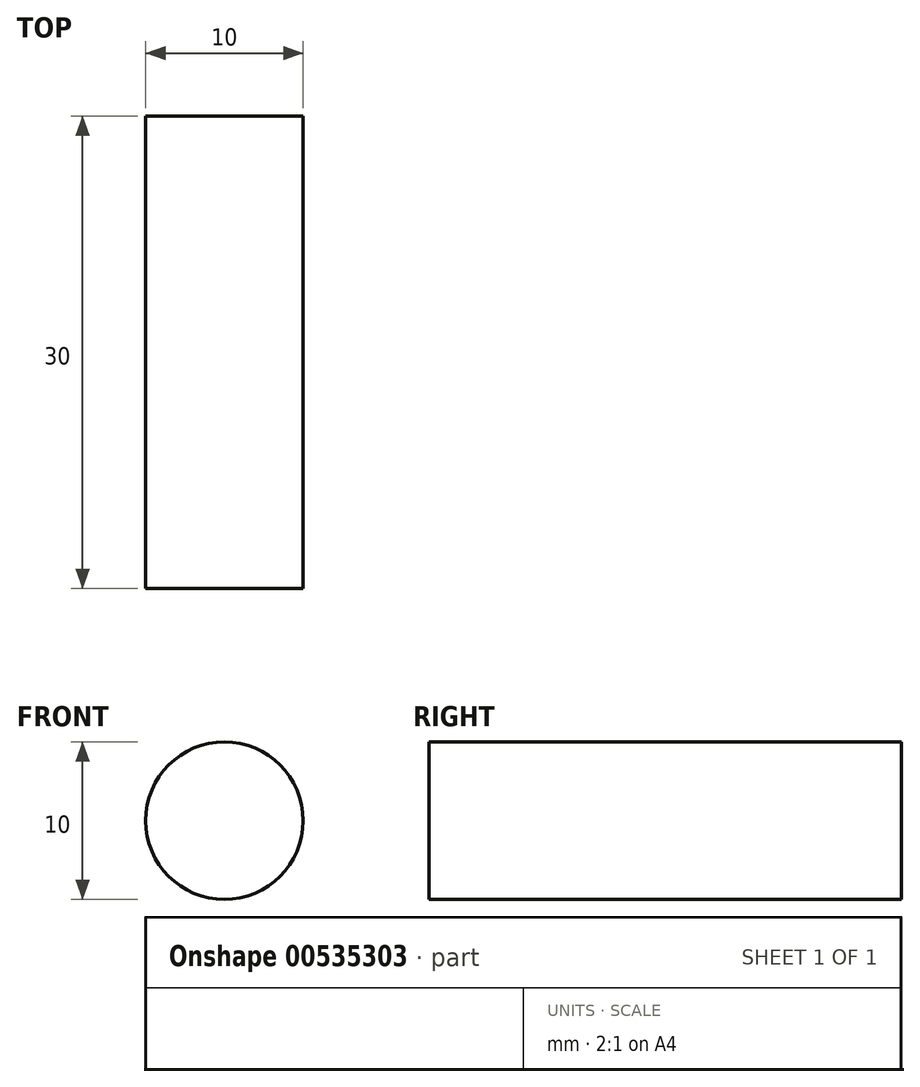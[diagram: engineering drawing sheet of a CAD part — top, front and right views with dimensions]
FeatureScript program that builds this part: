
annotation { "Feature Type Name" : "Feature", "Feature Type Description" : "" }
export const myFeature = defineFeature(function(context is Context, id is Id, definition is map)
    precondition{}
    {
        {
            var Q0;
            Q0=qCreatedBy(makeId("Front.planeOp"),FACE);
            var sketch = newSketch(context, id + "F0", { "sketchPlane" : qUnion([Q0])});
            skCircle(sketch, "E0", {"center": v(0, 0) * mm, "radius": 5 * mm});
            skSolve(sketch);
        }
        {
            var Q0;
            Q0=makeQuery(id+"F0.imprint","IMPRINT",FACE,{"disambiguationData":[TD([[makeQuery(id+"F0.imprint","IMPRINT",EDGE,{"derivedFrom":sQuery(id+"F0.wireOp",EDGE,"E0")}),1.0]])]});
            extrude(context, id + "F1", {"entities" : qUnion([Q0]), "depth" : 30 * mm, "offsetDistance" : 25 * mm});
        }
    });
